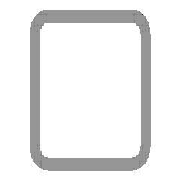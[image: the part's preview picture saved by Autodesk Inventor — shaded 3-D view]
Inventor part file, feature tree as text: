
AUTODESK INVENTOR PART (.ipt)
format: ipt  version: 2017 (Build 210142000, 142)  size: 133,120 bytes
history: native  units: mm (DEFAULTED — no unit token found)
features: other x4, plane x3, sketch x3, split x2
ambient origin geometry x8: Origin, YZ Plane, XZ Plane, XY Plane, X Axis, Y Axis, Z Axis, Center Point
bodies: Solid1 (feature_tree), Body (feature_tree)
feature tree (12):
  parser-record x1  (decoder bookkeeping rows leaked as tree rows — omitted from the tree; the rows remain in map.json)
  other  "Driven Length"
  other  "Start plane"
  other  "End plane"
  plane  "Work Plane4"
  split  "Split1"
  plane  "Work Plane5"
  split  "Split2"
  sketch  "Sketch"  dims[d10=76.2mm d11=76.2mm d12=6.35mm d13=203.2mm d14=889.0mm d15=38.1mm d16=38.1mm d17=12.7mm d18=90.0deg d19=685.8mm]
  sketch  "Sketch3"  dims[d3=685.8mm]
  plane  "Work Plane3"
  sketch  "Sketch4"  dims[d4=0.0mm]
